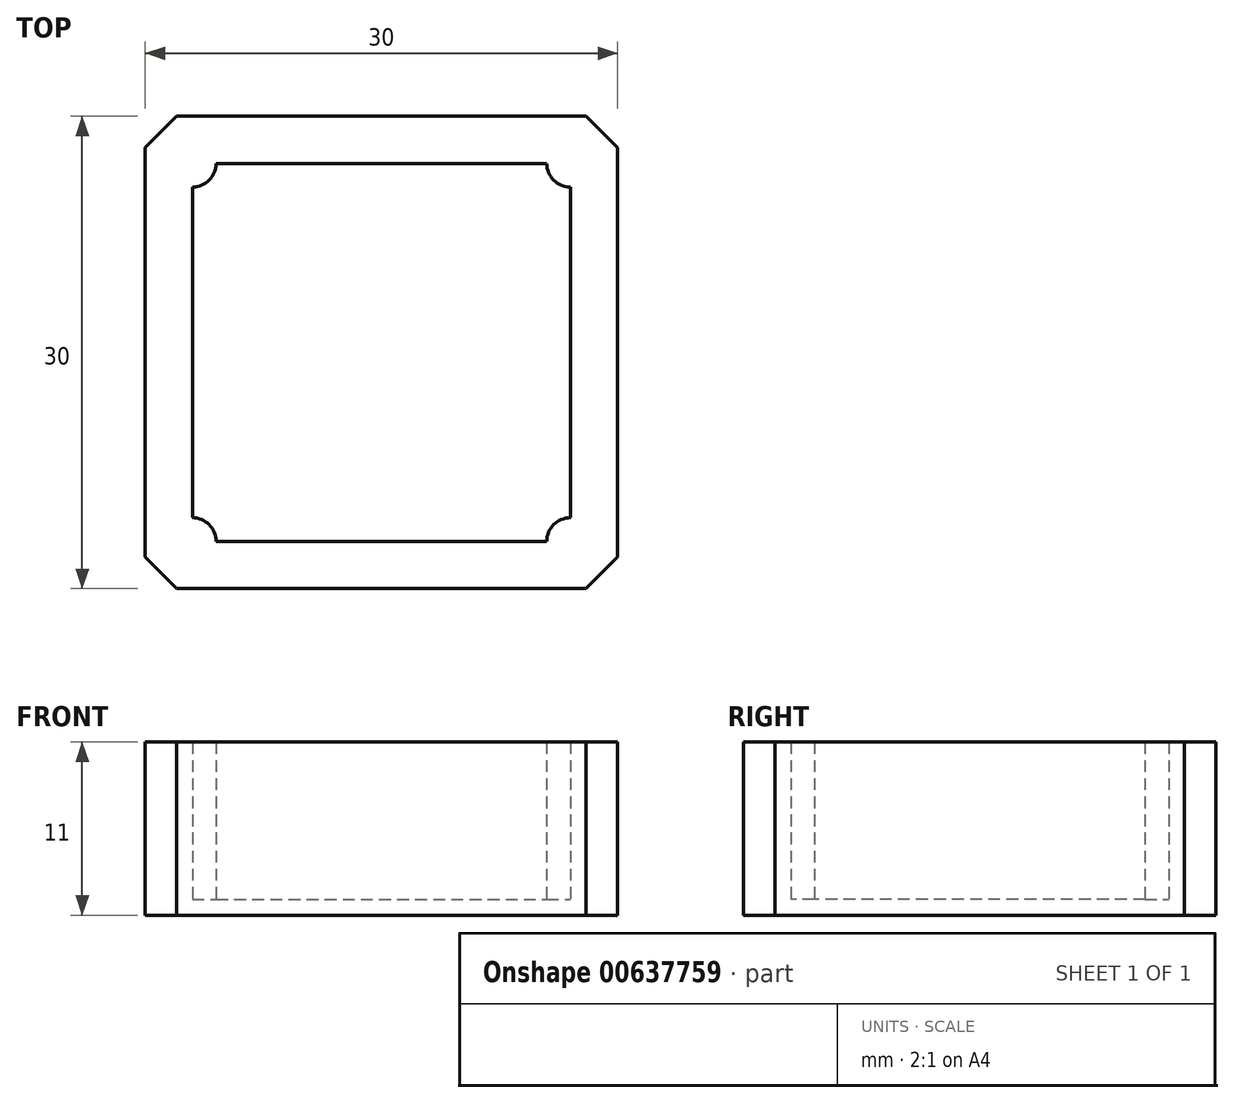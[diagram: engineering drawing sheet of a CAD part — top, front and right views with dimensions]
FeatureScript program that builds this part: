
annotation { "Feature Type Name" : "Feature", "Feature Type Description" : "" }
export const myFeature = defineFeature(function(context is Context, id is Id, definition is map)
    precondition{}
    {
        {
            var Q0;
            Q0=qCreatedBy(makeId("Top.planeOp"),FACE);
            var sketch = newSketch(context, id + "F0", { "sketchPlane" : qUnion([Q0])});
            skLineSegment(sketch, "E0.bottom", {"start": v(0, 30) * mm, "end": v(30, 30) * mm});
            skLineSegment(sketch, "E0.top", {"start": v(0, 0) * mm, "end": v(30, 0) * mm});
            skLineSegment(sketch, "E0.left", {"start": v(0, 30) * mm, "end": v(0, 0) * mm});
            skLineSegment(sketch, "E0.right", {"start": v(30, 30) * mm, "end": v(30, 0) * mm});
            skSolve(sketch);
        }
        {
            var Q0;
            Q0 = qSketchRegion(id + "F0", true);
            extrude(context, id + "F1", {"entities" : qUnion([Q0]), "depth" : 1 * mm, "offsetDistance" : 25.4 * mm});
        }
        {
            var Q0;
            Q0=makeQuery(id+"F1.opExtrude","CAP_FACE",FACE,{"disambiguationData":[OSD([sQuery(id+"F0.wireOp",EDGE,"E0.bottom"),sQuery(id+"F0.wireOp",EDGE,"E0.top"),sQuery(id+"F0.wireOp",EDGE,"E0.left"),sQuery(id+"F0.wireOp",EDGE,"E0.right")])],"isStart":false});
            var sketch = newSketch(context, id + "F2", { "sketchPlane" : qUnion([Q0])});
            skLineSegment(sketch, "E1.0", {"start": v(3, 25.5) * mm, "end": v(3, 4.5) * mm});
            skLineSegment(sketch, "E1.1", {"start": v(4.5, 27) * mm, "end": v(25.5, 27) * mm});
            skLineSegment(sketch, "E1.2", {"start": v(27, 25.5) * mm, "end": v(27, 4.5) * mm});
            skLineSegment(sketch, "E1.3", {"start": v(4.5, 3) * mm, "end": v(25.5, 3) * mm});
            skLineSegment(sketch, "E2.0", {"start": v(0, 30) * mm, "end": v(30, 30) * mm});
            skLineSegment(sketch, "E2.1", {"start": v(0, 30) * mm, "end": v(0, 0) * mm});
            skLineSegment(sketch, "E2.2", {"start": v(0, 0) * mm, "end": v(30, 0) * mm});
            skLineSegment(sketch, "E2.3", {"start": v(30, 30) * mm, "end": v(30, 0) * mm});
            skArc(sketch, "E3", {"start": v(3, 25.5) * mm, "mid": v(4.06, 25.94) * mm, "end": v(4.5, 27) * mm});
            skArc(sketch, "E4", {"start": v(25.5, 27) * mm, "mid": v(25.94, 25.94) * mm, "end": v(27, 25.5) * mm});
            skArc(sketch, "E5", {"start": v(4.5, 3) * mm, "mid": v(4.06, 4.06) * mm, "end": v(3, 4.5) * mm});
            skArc(sketch, "E6", {"start": v(27, 4.5) * mm, "mid": v(25.94, 4.06) * mm, "end": v(25.5, 3) * mm});
            skSolve(sketch);
        }
        {
            var Q0;
            Q0 = qSketchRegion(id + "F2", true);
            extrude(context, id + "F3", {"entities" : qUnion([Q0]), "operationType" : NewBodyOperationType.ADD, "depth" : 10 * mm, "offsetDistance" : 25.4 * mm});
        }
        {
            var Q0;
            Q0=makeQuery(id+"F3.boolean.opBoolean","MERGE",EDGE,{"derivedFrom":[makeQuery(id+"F1.opExtrude","SWEPT_EDGE",EDGE,{"disambiguationData":[OSD([sQuery(id+"F0.wireOp",EDGE,"E0.bottom"),sQuery(id+"F0.wireOp",EDGE,"E0.right")])]}),makeQuery(id+"F3.opExtrude","SWEPT_EDGE",EDGE,{"disambiguationData":[OSD([sQuery(id+"F2.wireOp",EDGE,"E2.0"),sQuery(id+"F2.wireOp",EDGE,"E2.3")])]})]});
            var Q1;
            Q1=makeQuery(id+"F3.boolean.opBoolean","MERGE",EDGE,{"derivedFrom":[makeQuery(id+"F1.opExtrude","SWEPT_EDGE",EDGE,{"disambiguationData":[OSD([sQuery(id+"F0.wireOp",EDGE,"E0.top"),sQuery(id+"F0.wireOp",EDGE,"E0.right")])]}),makeQuery(id+"F3.opExtrude","SWEPT_EDGE",EDGE,{"disambiguationData":[OSD([sQuery(id+"F2.wireOp",EDGE,"E2.2"),sQuery(id+"F2.wireOp",EDGE,"E2.3")])]})]});
            var Q2;
            Q2=makeQuery(id+"F3.boolean.opBoolean","MERGE",EDGE,{"derivedFrom":[makeQuery(id+"F1.opExtrude","SWEPT_EDGE",EDGE,{"disambiguationData":[OSD([sQuery(id+"F0.wireOp",EDGE,"E0.top"),sQuery(id+"F0.wireOp",EDGE,"E0.left")])]}),makeQuery(id+"F3.opExtrude","SWEPT_EDGE",EDGE,{"disambiguationData":[OSD([sQuery(id+"F2.wireOp",EDGE,"E2.1"),sQuery(id+"F2.wireOp",EDGE,"E2.2")])]})]});
            var Q3;
            Q3=makeQuery(id+"F3.boolean.opBoolean","MERGE",EDGE,{"derivedFrom":[makeQuery(id+"F1.opExtrude","SWEPT_EDGE",EDGE,{"disambiguationData":[OSD([sQuery(id+"F0.wireOp",EDGE,"E0.bottom"),sQuery(id+"F0.wireOp",EDGE,"E0.left")])]}),makeQuery(id+"F3.opExtrude","SWEPT_EDGE",EDGE,{"disambiguationData":[OSD([sQuery(id+"F2.wireOp",EDGE,"E2.0"),sQuery(id+"F2.wireOp",EDGE,"E2.1")])]})]});
            chamfer(context, id + "F4", {"entities" : qUnion([Q0, Q1, Q2, Q3]), "width" : 2 * mm, "tangentPropagation" : true});
        }
    });
